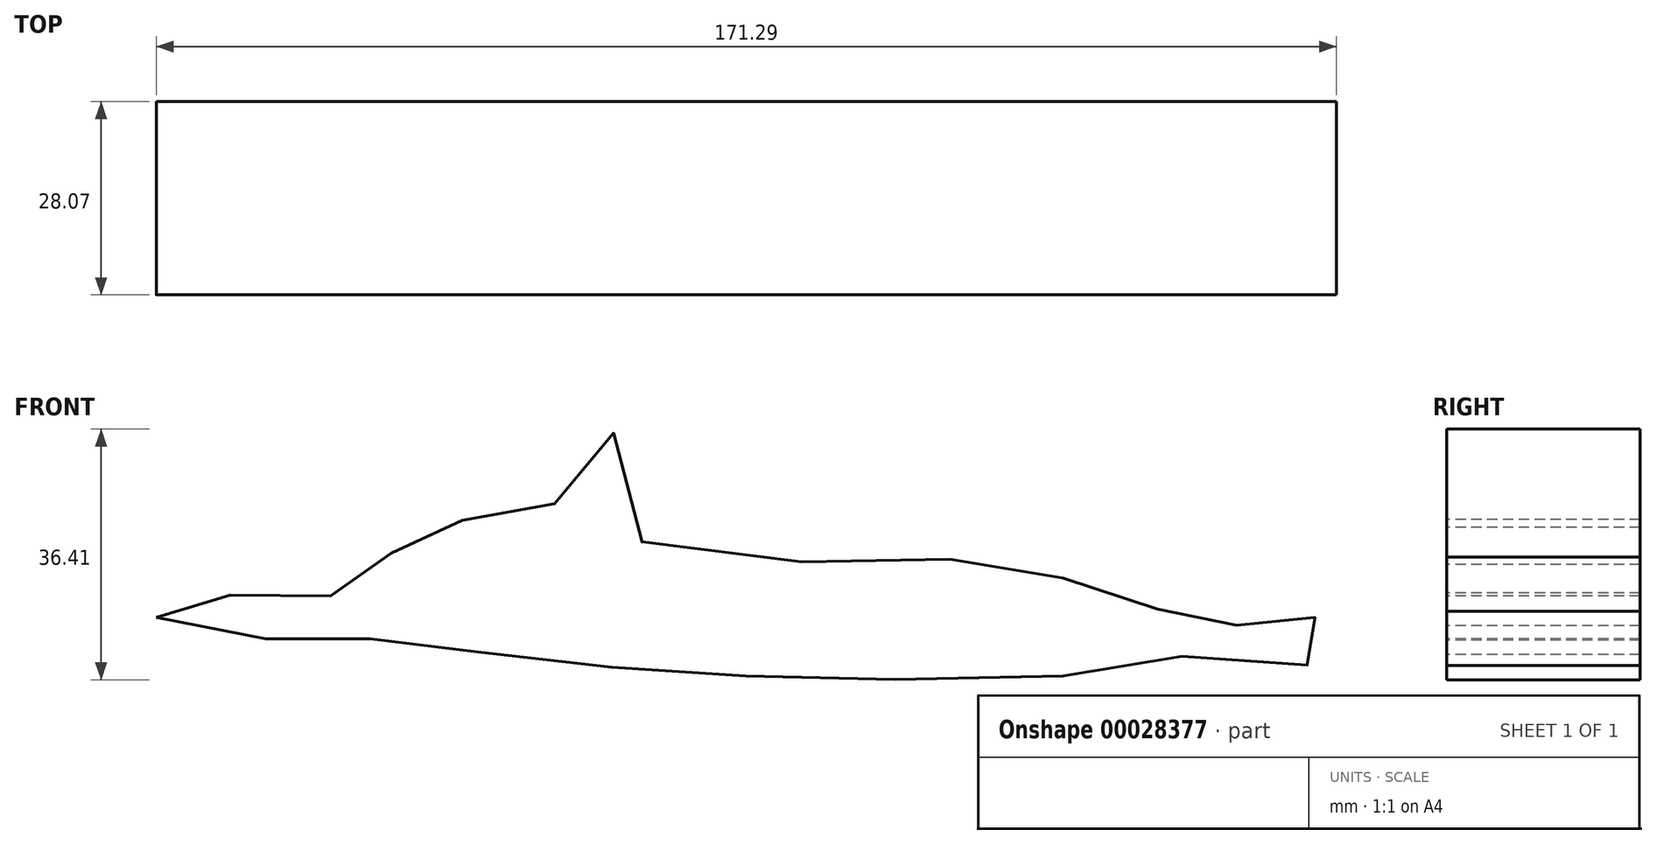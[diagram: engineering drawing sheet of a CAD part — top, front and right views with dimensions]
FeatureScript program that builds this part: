
annotation { "Feature Type Name" : "Feature", "Feature Type Description" : "" }
export const myFeature = defineFeature(function(context is Context, id is Id, definition is map)
    precondition{}
    {
        {
            var Q0;
            Q0=qCreatedBy(makeId("Front.planeOp"),FACE);
            var sketch = newSketch(context, id + "F0", { "sketchPlane" : qUnion([Q0])});
            skFitSpline(sketch, "E0", {"points": [v(-96.69, 13.08) * mm, v(-91.15, 15.44) * mm, v(-77.77, 16.57) * mm, v(-66.23, 17.28) * mm, v(-61.39, 24.12) * mm, v(-53.03, 27.26) * mm, v(-41.26, 27.5) * mm, v(-30.63, 40.41) * mm, v(-28.1, 26.04) * mm, v(5.6, 21.7) * mm, v(27.13, 20.31) * mm, v(43.85, 16.28) * mm, v(52.82, 12.69) * mm, v(62.27, 12.34) * mm, v(70.68, 13.55) * mm, v(74.34, 7.12) * mm, v(57.86, 7.62) * mm, v(40.2, 5.16) * mm, v(3.54, 4.2) * mm, v(-22.74, 5.2) * mm, v(-48.36, 7.83) * mm, v(-65.02, 9.93) * mm, v(-79.21, 9.9) * mm, v(-96.69, 13.08) * mm]});
            skSolve(sketch);
        }
        {
            var Q0;
            Q0=makeQuery(id+"F0.imprint","IMPRINT",FACE,{"disambiguationData":[TD([[makeQuery(id+"F0.imprint","IMPRINT",EDGE,{"derivedFrom":sQuery(id+"F0.wireOp",EDGE,"E0")}),-1.0]])]});
            extrude(context, id + "F1", {"entities" : qUnion([Q0]), "oppositeDirection" : true, "depth" : 28.07 * mm});
        }
    });
